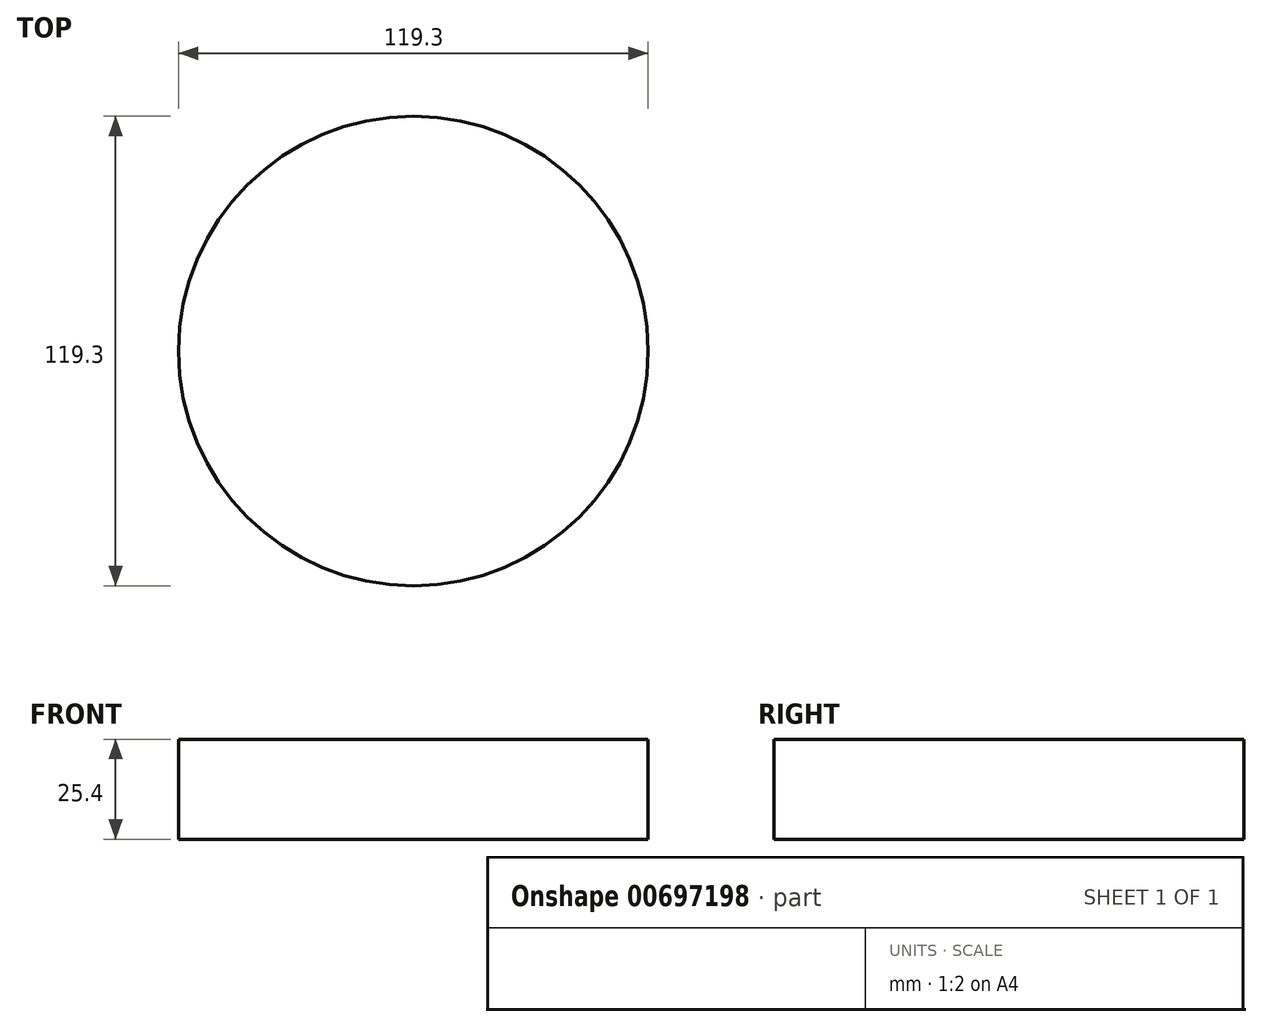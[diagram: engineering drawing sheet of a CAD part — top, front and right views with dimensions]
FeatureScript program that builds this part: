
annotation { "Feature Type Name" : "Feature", "Feature Type Description" : "" }
export const myFeature = defineFeature(function(context is Context, id is Id, definition is map)
    precondition{}
    {
        {
            var Q0;
            Q0=qCreatedBy(makeId("Top.planeOp"),FACE);
            var sketch = newSketch(context, id + "F0", { "sketchPlane" : qUnion([Q0])});
            skCircle(sketch, "E0", {"center": v(0, 0) * mm, "radius": 59.65 * mm});
            skSolve(sketch);
        }
        {
            var Q0;
            Q0=makeQuery(id+"F0.imprint","IMPRINT",FACE,{"disambiguationData":[TD([[makeQuery(id+"F0.imprint","IMPRINT",EDGE,{"derivedFrom":sQuery(id+"F0.wireOp",EDGE,"E0")}),1.0]])]});
            extrude(context, id + "F1", {"entities" : qUnion([Q0]), "depth" : 25.4 * mm, "offsetDistance" : 25.4 * mm});
        }
    });
